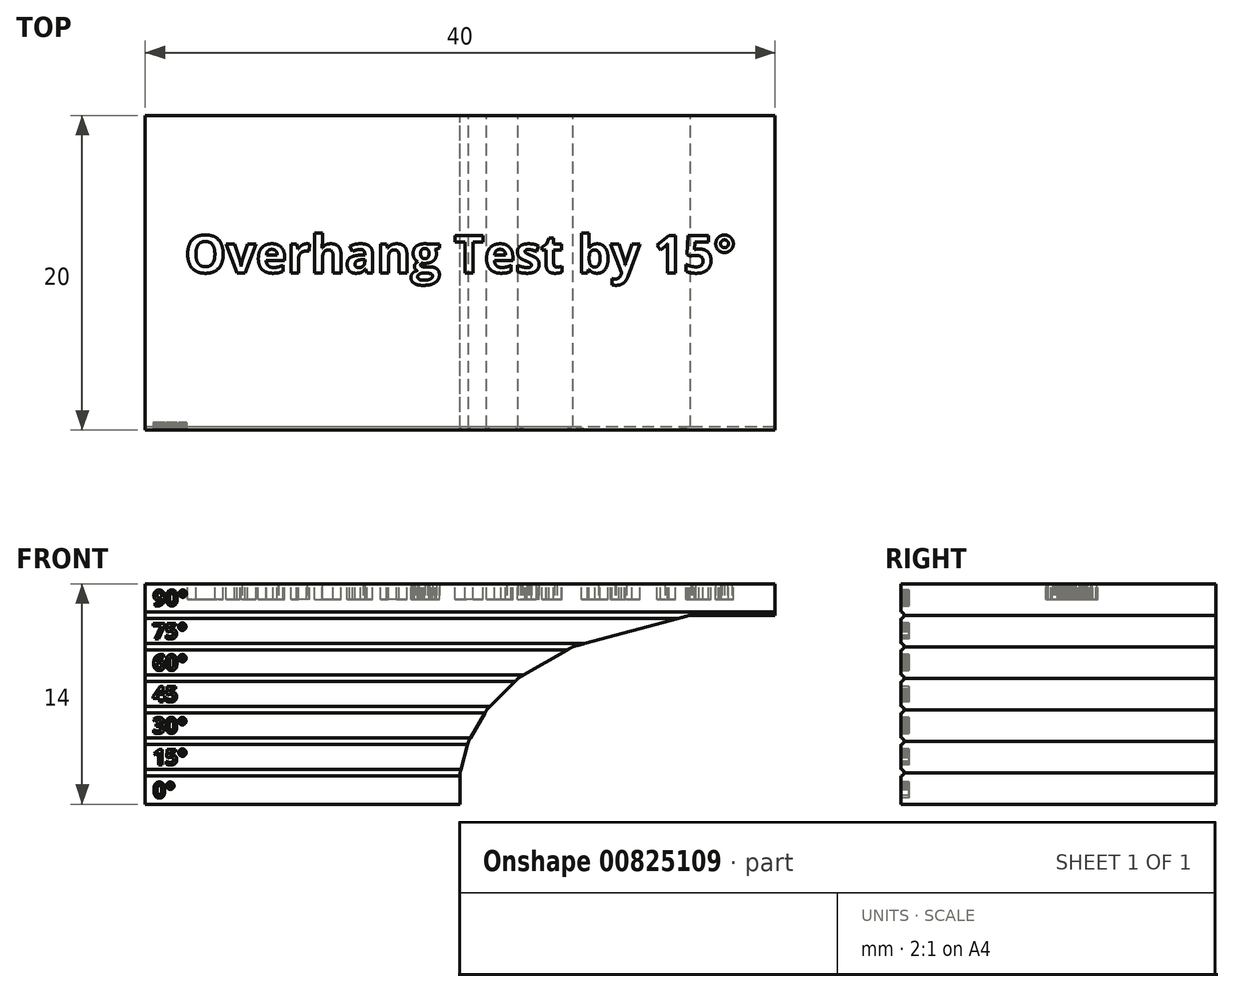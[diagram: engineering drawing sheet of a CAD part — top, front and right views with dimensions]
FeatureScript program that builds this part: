
annotation { "Feature Type Name" : "Feature", "Feature Type Description" : "" }
export const myFeature = defineFeature(function(context is Context, id is Id, definition is map)
    precondition{}
    {
        {
            var Q0;
            Q0=qCreatedBy(makeId("Front.planeOp"),FACE);
            var sketch = newSketch(context, id + "F0", { "sketchPlane" : qUnion([Q0])});
            skLineSegment(sketch, "E0", {"start": v(0, 0) * mm, "end": v(20, 0) * mm});
            skLineSegment(sketch, "E1", {"start": v(20, 0) * mm, "end": v(20, 2) * mm});
            skLineSegment(sketch, "E2", {"start": v(20, 2) * mm, "end": v(20.54, 4) * mm});
            skLineSegment(sketch, "E3", {"start": v(20.54, 4) * mm, "end": v(21.7, 6) * mm});
            skLineSegment(sketch, "E4", {"start": v(21.7, 6) * mm, "end": v(23.7, 8) * mm});
            skLineSegment(sketch, "E5", {"start": v(23.7, 8) * mm, "end": v(27.15, 10) * mm});
            skLineSegment(sketch, "E6", {"start": v(40, 14) * mm, "end": v(0, 14) * mm});
            skLineSegment(sketch, "E7", {"start": v(0, 14) * mm, "end": v(0, 0) * mm});
            skLineSegment(sketch, "E8", {"start": v(27.15, 10) * mm, "end": v(34.62, 12) * mm});
            skLineSegment(sketch, "E9", {"start": v(20, 2) * mm, "end": v(34.62, 2) * mm, "construction": true});
            skLineSegment(sketch, "E10", {"start": v(20, 0) * mm, "end": v(34.62, 0) * mm, "construction": true});
            skLineSegment(sketch, "E11", {"start": v(20.54, 4) * mm, "end": v(34.62, 4) * mm, "construction": true});
            skLineSegment(sketch, "E12", {"start": v(21.7, 6) * mm, "end": v(34.62, 6) * mm, "construction": true});
            skLineSegment(sketch, "E13", {"start": v(23.7, 8) * mm, "end": v(34.62, 8) * mm, "construction": true});
            skLineSegment(sketch, "E14", {"start": v(27.15, 10) * mm, "end": v(34.62, 10) * mm, "construction": true});
            skLineSegment(sketch, "E15", {"start": v(34.62, 12) * mm, "end": v(34.62, 10) * mm, "construction": true});
            skLineSegment(sketch, "E16", {"start": v(34.62, 8) * mm, "end": v(34.62, 6) * mm, "construction": true});
            skLineSegment(sketch, "E17", {"start": v(34.62, 8) * mm, "end": v(34.62, 10) * mm, "construction": true});
            skLineSegment(sketch, "E18", {"start": v(34.62, 6) * mm, "end": v(34.62, 4) * mm, "construction": true});
            skLineSegment(sketch, "E19", {"start": v(34.62, 4) * mm, "end": v(34.62, 2) * mm, "construction": true});
            skLineSegment(sketch, "E20", {"start": v(34.62, 2) * mm, "end": v(34.62, 0) * mm, "construction": true});
            skLineSegment(sketch, "E21", {"start": v(34.62, 12) * mm, "end": v(40, 12) * mm});
            skLineSegment(sketch, "E22", {"start": v(40, 12) * mm, "end": v(40, 14) * mm});
            skSolve(sketch);
        }
        {
            var Q0;
            Q0=makeQuery(id+"F0.imprint","IMPRINT",FACE,{"disambiguationData":[TD([[makeQuery(id+"F0.imprint","IMPRINT",EDGE,{"derivedFrom":sQuery(id+"F0.wireOp",EDGE,"E0")}),1.0]])]});
            extrude(context, id + "F1", {"entities" : qUnion([Q0]), "depth" : 20 * mm, "offsetDistance" : 25 * mm});
        }
        {
            var Q0;
            Q0=makeQuery(id+"F1.opExtrude","SWEPT_FACE",FACE,{"disambiguationData":[OSD([sQuery(id+"F0.wireOp",EDGE,"E7")])]});
            var sketch = newSketch(context, id + "F2", { "sketchPlane" : qUnion([Q0])});
            skPoint(sketch, "E23.0", {"position": v(20, 2) * mm});
            skPoint(sketch, "E23.1", {"position": v(20, 4) * mm});
            skPoint(sketch, "E23.2", {"position": v(20, 6) * mm});
            skPoint(sketch, "E23.3", {"position": v(20, 8) * mm});
            skPoint(sketch, "E23.4", {"position": v(20, 10) * mm});
            skPoint(sketch, "E23.5", {"position": v(20, 10) * mm});
            skArc(sketch, "E24", {"start": v(20, 2.2) * mm, "mid": v(19.8, 2) * mm, "end": v(20, 1.8) * mm});
            skArc(sketch, "E25", {"start": v(20, 4.2) * mm, "mid": v(19.8, 4) * mm, "end": v(20, 3.8) * mm});
            skArc(sketch, "E26", {"start": v(20, 6.2) * mm, "mid": v(19.8, 6) * mm, "end": v(20, 5.8) * mm});
            skArc(sketch, "E27", {"start": v(20, 8.2) * mm, "mid": v(19.8, 8) * mm, "end": v(20, 7.8) * mm});
            skArc(sketch, "E28", {"start": v(20, 10.2) * mm, "mid": v(19.8, 10) * mm, "end": v(20, 9.8) * mm});
            skPoint(sketch, "E29.0", {"position": v(20, 12) * mm});
            skArc(sketch, "E30", {"start": v(20, 12.2) * mm, "mid": v(19.8, 12) * mm, "end": v(20, 11.8) * mm});
            skSolve(sketch);
        }
        {
            var Q0;
            {var subQ0=sQuery(id+"F2.wireOp",EDGE,"E28");Q0=makeQuery(id+"F2.imprint","IMPRINT",FACE,{"disambiguationData":[TD([[makeQuery(id+"F2.imprint","IMPRINT",EDGE,{"derivedFrom":subQ0}),1.0]])]});}
            var Q1;
            {var subQ0=sQuery(id+"F2.wireOp",EDGE,"E27");Q1=makeQuery(id+"F2.imprint","IMPRINT",FACE,{"disambiguationData":[TD([[makeQuery(id+"F2.imprint","IMPRINT",EDGE,{"derivedFrom":subQ0}),1.0]])]});}
            var Q2;
            {var subQ0=sQuery(id+"F2.wireOp",EDGE,"E26");Q2=makeQuery(id+"F2.imprint","IMPRINT",FACE,{"disambiguationData":[TD([[makeQuery(id+"F2.imprint","IMPRINT",EDGE,{"derivedFrom":subQ0}),1.0]])]});}
            var Q3;
            {var subQ0=sQuery(id+"F2.wireOp",EDGE,"E25");Q3=makeQuery(id+"F2.imprint","IMPRINT",FACE,{"disambiguationData":[TD([[makeQuery(id+"F2.imprint","IMPRINT",EDGE,{"derivedFrom":subQ0}),1.0]])]});}
            var Q4;
            {var subQ0=sQuery(id+"F2.wireOp",EDGE,"E24");Q4=makeQuery(id+"F2.imprint","IMPRINT",FACE,{"disambiguationData":[TD([[makeQuery(id+"F2.imprint","IMPRINT",EDGE,{"derivedFrom":subQ0}),1.0]])]});}
            var Q5;
            {var subQ0=sQuery(id+"F2.wireOp",EDGE,"E30");Q5=makeQuery(id+"F2.imprint","IMPRINT",FACE,{"disambiguationData":[TD([[makeQuery(id+"F2.imprint","IMPRINT",EDGE,{"derivedFrom":subQ0}),1.0]])]});}
            extrude(context, id + "F3", {"entities" : qUnion([Q0, Q1, Q2, Q3, Q4, Q5]), "operationType" : NewBodyOperationType.REMOVE, "endBound" : BoundingType.THROUGH_ALL, "oppositeDirection" : true, "depth" : 25 * mm, "offsetDistance" : 25 * mm});
        }
        {
            var Q0;
            {var subQ0=sQuery(id+"F0.wireOp",EDGE,"E0");var subQ1=sQuery(id+"F0.wireOp",EDGE,"E1");var subQ2=sQuery(id+"F0.wireOp",EDGE,"E7");Q0=makeQuery(id+"F3.boolean.opBoolean","SPLIT",FACE,{"disambiguationData":[TD([makeQuery(id+"F1.opExtrude","SWEPT_FACE",FACE,{"disambiguationData":[OSD([subQ0])]})])],"derivedFrom":makeQuery(id+"F1.opExtrude","CAP_FACE",FACE,{"disambiguationData":[OSD([subQ0,subQ1,sQuery(id+"F0.wireOp",EDGE,"E2"),sQuery(id+"F0.wireOp",EDGE,"E3"),sQuery(id+"F0.wireOp",EDGE,"E4"),sQuery(id+"F0.wireOp",EDGE,"E5"),sQuery(id+"F0.wireOp",EDGE,"E6"),subQ2,sQuery(id+"F0.wireOp",EDGE,"E8"),sQuery(id+"F0.wireOp",EDGE,"E21"),sQuery(id+"F0.wireOp",EDGE,"E22")])],"isStart":false})});}
            var sketch = newSketch(context, id + "F4", { "sketchPlane" : qUnion([Q0])});
            skPoint(sketch, "E31.0", {"position": v(0, 3.8) * mm});
            skPoint(sketch, "E31.1", {"position": v(0, 2.2) * mm});
            skPoint(sketch, "E31.2", {"position": v(0, 4.2) * mm});
            skPoint(sketch, "E31.3", {"position": v(0, 5.8) * mm});
            skPoint(sketch, "E31.4", {"position": v(0, 6.2) * mm});
            skPoint(sketch, "E31.5", {"position": v(0, 7.8) * mm});
            skPoint(sketch, "E31.6", {"position": v(0, 8.2) * mm});
            skPoint(sketch, "E31.7", {"position": v(0, 9.8) * mm});
            skPoint(sketch, "E31.8", {"position": v(0, 10.2) * mm});
            skPoint(sketch, "E31.9", {"position": v(0, 11.8) * mm});
            skPoint(sketch, "E31.10", {"position": v(0, 12.2) * mm});
            skPoint(sketch, "E31.11", {"position": v(0, 14) * mm});
            skText(sketch, "E32", { "text": "0°", "fontName": "OpenSans-Bold.ttf"});
            skText(sketch, "E33", { "text": "15°", "fontName": "OpenSans-Bold.ttf"});
            skText(sketch, "E34", { "text": "30°", "fontName": "OpenSans-Bold.ttf"});
            skText(sketch, "E35", { "text": "45", "fontName": "OpenSans-Bold.ttf"});
            skText(sketch, "E36", { "text": "60°", "fontName": "OpenSans-Bold.ttf"});
            skText(sketch, "E37", { "text": "75°", "fontName": "OpenSans-Bold.ttf"});
            skText(sketch, "E38", { "text": "90°", "fontName": "OpenSans-Bold.ttf"});
            const initialGuessF4  = {"E32": [0.0005, 0.0004, 1, 0, 0.001], "E33": [0.00048, 0.0025, 1, 0, 0.001], "E34": [0.00047, 0.0045, 1, 0, 0.001], "E35": [0.00047, 0.0065, 1, 0, 0.001], "E36": [0.00048, 0.0085, 1, 0, 0.001], "E37": [0.00047, 0.0105, 1, 0, 0.001], "E38": [0.0005, 0.0126, 1, 0, 0.001]};
            skSetInitialGuess(sketch, initialGuessF4);
            skSolve(sketch);
        }
        {
            var Q0;
            Q0 = qSketchRegion(id + "F4", true);
            extrude(context, id + "F5", {"entities" : qUnion([Q0]), "operationType" : NewBodyOperationType.REMOVE, "oppositeDirection" : true, "depth" : .5 * mm, "offsetDistance" : 25 * mm});
        }
        {
            var Q0;
            Q0=makeQuery(id+"F1.opExtrude","SWEPT_FACE",FACE,{"disambiguationData":[OSD([sQuery(id+"F0.wireOp",EDGE,"E6")])]});
            var sketch = newSketch(context, id + "F6", { "sketchPlane" : qUnion([Q0])});
            skText(sketch, "E39", { "text": "Overhang Test by 15°", "fontName": "OpenSans-Bold.ttf"});
            const initialGuessF6  = {"E39": [0.0025, -0.01, 1, 0, 0.00239]};
            skSetInitialGuess(sketch, initialGuessF6);
            skSolve(sketch);
        }
        {
            var Q0;
            Q0 = qSketchRegion(id + "F6", true);
            extrude(context, id + "F7", {"entities" : qUnion([Q0]), "operationType" : NewBodyOperationType.REMOVE, "oppositeDirection" : true, "depth" : 1 * mm, "offsetDistance" : 25 * mm});
        }
    });
